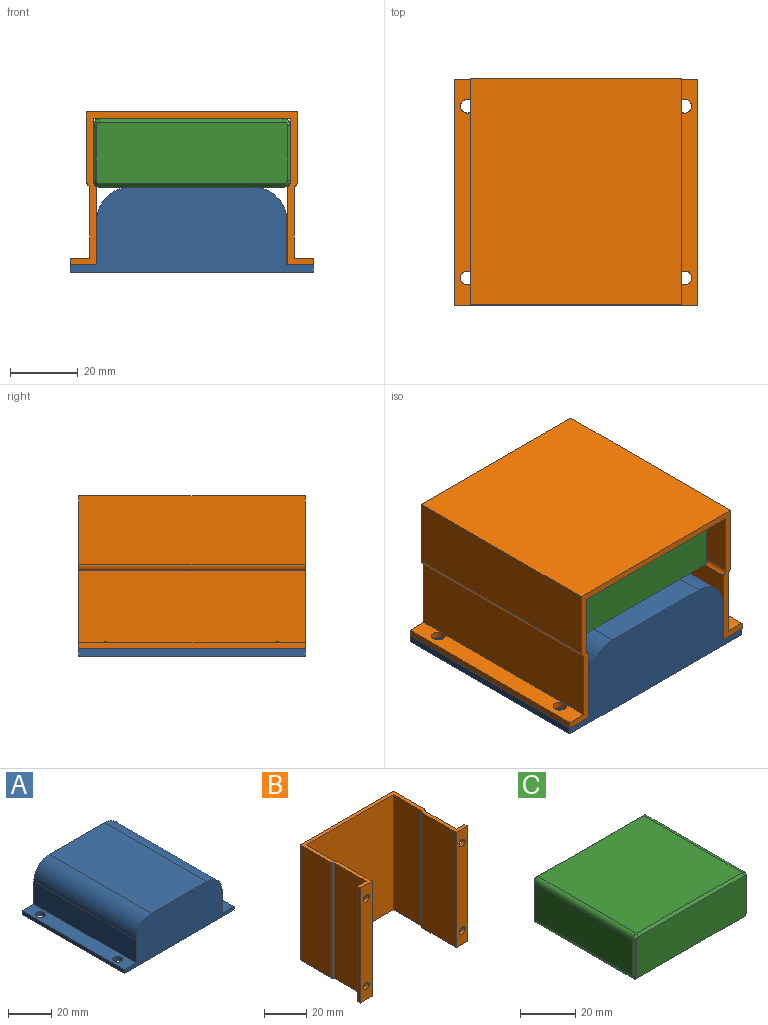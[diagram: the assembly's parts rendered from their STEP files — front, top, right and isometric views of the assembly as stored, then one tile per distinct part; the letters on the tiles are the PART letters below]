
ASSEMBLY  parts=3 mates=2
PART A: 16 faces, bbox 71.5x66.5x25 mm
  f0: plane 66.5x12.9mm, normal (1,0,0), area 857.9mm2, adj f1,f3,f7,f15
  f1: plane 71.5x25mm, normal (0,1,0), area 1389.6mm2, adj f0,f2,f4,f5,f6,f7,f8,f11
  f2: plane 66.5x12.9mm, normal (-1,0,0), area 857.9mm2, adj f1,f3,f6,f11
  f3: plane 71.5x25mm, normal (0,-1,0), area 1389.6mm2, adj f0,f2,f4,f5,f6,f7,f8,f11
  f4: plane 66.5x36mm, normal (0,0,1), area 2394mm2, adj f1,f3,f6,f7
  f5: plane 71.5x66.5mm, normal (0,0,-1), area 4691.1mm2, adj f1,f3,f8,f9,f10,f12,f13,f14
  f6: cylinder r=10mm len=66.5mm, axis (0,1,0), area 1044.6mm2, adj f1,f2,f3,f4
  f7: cylinder r=10mm len=66.5mm, axis (0,-1,0), area 1044.6mm2, adj f0,f1,f3,f4
  f8: plane 66.5x2.1mm, normal (-1,0,0), area 139.7mm2, adj f1,f3,f5,f11
  f9: cylinder r=2.25mm len=4.5mm, axis (0,0,-1), area 29.7mm2, adj f5,f11
  f10: cylinder r=2.25mm len=4.5mm, axis (0,0,-1), area 29.7mm2, adj f5,f11
  f11: plane 66.5x7.75mm, normal (0,0,1), area 483.6mm2, adj f1,f2,f3,f8,f9,f10
  f12: cylinder r=2.25mm len=4.5mm, axis (0,0,-1), area 29.7mm2, adj f5,f15
  f13: cylinder r=2.25mm len=4.5mm, axis (0,0,-1), area 29.7mm2, adj f5,f15
  f14: plane 66.5x2.1mm, normal (1,0,0), area 139.7mm2, adj f1,f3,f5,f15
  f15: plane 66.5x7.75mm, normal (0,0,1), area 483.6mm2, adj f0,f1,f3,f12,f13,f14
PART B: 30 faces, bbox 71.8x45.2x66.7 mm
  f0: plane 66.73x21.24mm, normal (1,0,0), area 1396.4mm2, adj f1,f25,f26,f27,f28,f29
  f1: plane 71.6x45mm, normal (0,0,1), area 319.2mm2, adj f0,f2,f3,f6,f7,f8,f9,f10
  f2: plane 66.5x2mm, normal (1,0,0), area 133mm2, adj f1,f3,f26,f29
  f3: plane 66.5x7.7mm, normal (0,-1,0), area 486.9mm2, adj f1,f2,f4,f5,f6,f26
  f4: cylinder r=2mm len=4mm, axis (0,-1,0), area 25.1mm2, adj f3,f27,f29
  f5: cylinder r=2mm len=4mm, axis (0,-1,0), area 25.1mm2, adj f3,f28,f29
  f6: plane 66.5x23mm, normal (-1,0,0), area 1529.5mm2, adj f1,f3,f7,f26
  f7: cylinder r=2mm len=66.5mm, axis (0,0,1), area 139.3mm2, adj f1,f6,f8,f26
  f8: plane 66.5x18.27mm, normal (-1,0,0), area 1214.8mm2, adj f1,f7,f9,f26
  f9: plane 66.5x58.2mm, normal (0,-1,0), area 3870.3mm2, adj f1,f8,f10,f26
  f10: plane 66.5x18.27mm, normal (1,0,0), area 1214.8mm2, adj f1,f9,f11,f26
  f11: cylinder r=2mm len=66.5mm, axis (0,0,-1), area 139.3mm2, adj f1,f10,f12,f26
  f12: plane 66.5x23mm, normal (1,0,0), area 1529.5mm2, adj f1,f11,f13,f26
  f13: plane 66.5x7.7mm, normal (0,-1,0), area 486.9mm2, adj f1,f12,f14,f16,f18,f26
  f14: cylinder r=2mm len=4mm, axis (0,-1,0), area 25.1mm2, adj f13,f15,f19
  f15: cone r=0mm half-angle=59deg, axis (0,-1,0), area 0mm2, adj f14,f20
  f16: cylinder r=2mm len=4mm, axis (0,-1,0), area 25.1mm2, adj f13,f17,f19
  f17: cone r=0mm half-angle=59deg, axis (0,-1,0), area 0mm2, adj f16,f20
  f18: plane 66.5x2mm, normal (-1,0,0), area 133mm2, adj f1,f13,f19,f26
  f19: plane 66.5x5.7mm, normal (0,1,0), area 354.1mm2, adj f1,f14,f16,f18,f20,f26
  f20: plane 66.73x21.24mm, normal (-1,0,0), area 1396.4mm2, adj f1,f15,f17,f19,f21,f26
  f21: cylinder r=2mm len=66.5mm, axis (0,0,1), area 139.3mm2, adj f1,f20,f22,f26
  f22: plane 66.5x20.27mm, normal (-1,0,0), area 1347.8mm2, adj f1,f21,f23,f26
  f23: plane 66.5x62.2mm, normal (0,1,0), area 4136.3mm2, adj f1,f22,f24,f26
  f24: plane 66.5x20.27mm, normal (1,0,0), area 1347.8mm2, adj f1,f23,f25,f26
  f25: cylinder r=2mm len=66.5mm, axis (0,0,-1), area 139.3mm2, adj f0,f1,f24,f26
  f26: plane 71.6x45mm, normal (0,0,-1), area 319.2mm2, adj f0,f2,f3,f6,f7,f8,f9,f10
  f27: cone r=0mm half-angle=59deg, axis (0,-1,0), area 0mm2, adj f0,f4
  f28: cone r=0mm half-angle=59deg, axis (0,-1,0), area 0mm2, adj f0,f5
  f29: plane 66.5x5.7mm, normal (0,1,0), area 354.1mm2, adj f0,f1,f2,f4,f5,f26
PART C: 26 faces, bbox 58.2x52.7x20.1 mm
  f0: plane 56.15x18.1mm, normal (0,1,0), area 1015.5mm2, adj f10,f11,f12,f13,f14,f15,f16,f17
  f1: plane 50.7x16.1mm, normal (-1,0,0), area 816.3mm2, adj f6,f8,f13,f21
  f2: plane 56.15x18.1mm, normal (0,-1,0), area 1015.5mm2, adj f18,f19,f20,f21,f22,f23,f24,f25
  f3: plane 50.7x16.1mm, normal (1,0,0), area 816.3mm2, adj f7,f9,f14,f22
  f4: plane 54.15x50.7mm, normal (0,0,1), area 2745.4mm2, adj f8,f9,f10,f18
  f5: plane 54.15x50.7mm, normal (0,0,-1), area 2745.4mm2, adj f6,f7,f17,f25
  f6: cylinder r=2mm len=50.7mm, axis (0,-1,0), area 159.3mm2, adj f1,f5,f15,f23
  f7: cylinder r=2mm len=50.7mm, axis (0,1,0), area 159.3mm2, adj f3,f5,f16,f24
  f8: cylinder r=2mm len=50.7mm, axis (0,1,0), area 159.3mm2, adj f1,f4,f11,f19
  f9: cylinder r=2mm len=50.7mm, axis (0,-1,0), area 159.3mm2, adj f3,f4,f12,f20
  f10: plane 54.15x1mm, normal (0,0.71,0.71), area 76.6mm2, adj f0,f4,f11,f12
  f11: cone r=1mm half-angle=45deg, axis (0,-1,0), area 3.3mm2, adj f0,f8,f10,f13
  f12: cone r=1mm half-angle=45deg, axis (0,-1,0), area 3.3mm2, adj f0,f9,f10,f14
  f13: plane 16.1x1mm, normal (-0.71,0.71,0), area 22.8mm2, adj f0,f1,f11,f15
  f14: plane 16.1x1mm, normal (0.71,0.71,0), area 22.8mm2, adj f0,f3,f12,f16
  f15: cone r=1mm half-angle=45deg, axis (0,-1,0), area 3.3mm2, adj f0,f6,f13,f17
  f16: cone r=1mm half-angle=45deg, axis (0,-1,0), area 3.3mm2, adj f0,f7,f14,f17
  f17: plane 54.15x1mm, normal (0,0.71,-0.71), area 76.6mm2, adj f0,f5,f15,f16
  f18: plane 54.15x1mm, normal (0,-0.71,0.71), area 76.6mm2, adj f2,f4,f19,f20
  f19: cone r=1mm half-angle=45deg, axis (0,1,0), area 3.3mm2, adj f2,f8,f18,f21
  f20: cone r=1mm half-angle=45deg, axis (0,1,0), area 3.3mm2, adj f2,f9,f18,f22
  f21: plane 16.1x1mm, normal (-0.71,-0.71,0), area 22.8mm2, adj f1,f2,f19,f23
  f22: plane 16.1x1mm, normal (0.71,-0.71,0), area 22.8mm2, adj f2,f3,f20,f24
  f23: cone r=1mm half-angle=45deg, axis (0,1,0), area 3.3mm2, adj f2,f6,f21,f25
  f24: cone r=1mm half-angle=45deg, axis (0,1,0), area 3.3mm2, adj f2,f7,f22,f25
  f25: plane 54.15x1mm, normal (0,-0.71,-0.71), area 76.6mm2, adj f2,f5,f23,f24
PLACE A t=(-8.62,-9.34,-59.76)mm
PLACE B rot(axis=(1,0,0),90deg) t=(-8.55,23.91,-36.16)mm
PLACE C t=(-8.62,-9.34,-34.76)mm
MATE fastened B.f13 <-> A.f11  axis (0,0,-1) through (-40.5,-9.34,-57.66)mm
MATE fastened C.f5 <-> A.f4  axis (0,0,-1) through (-8.62,-9.34,-34.76)mm
